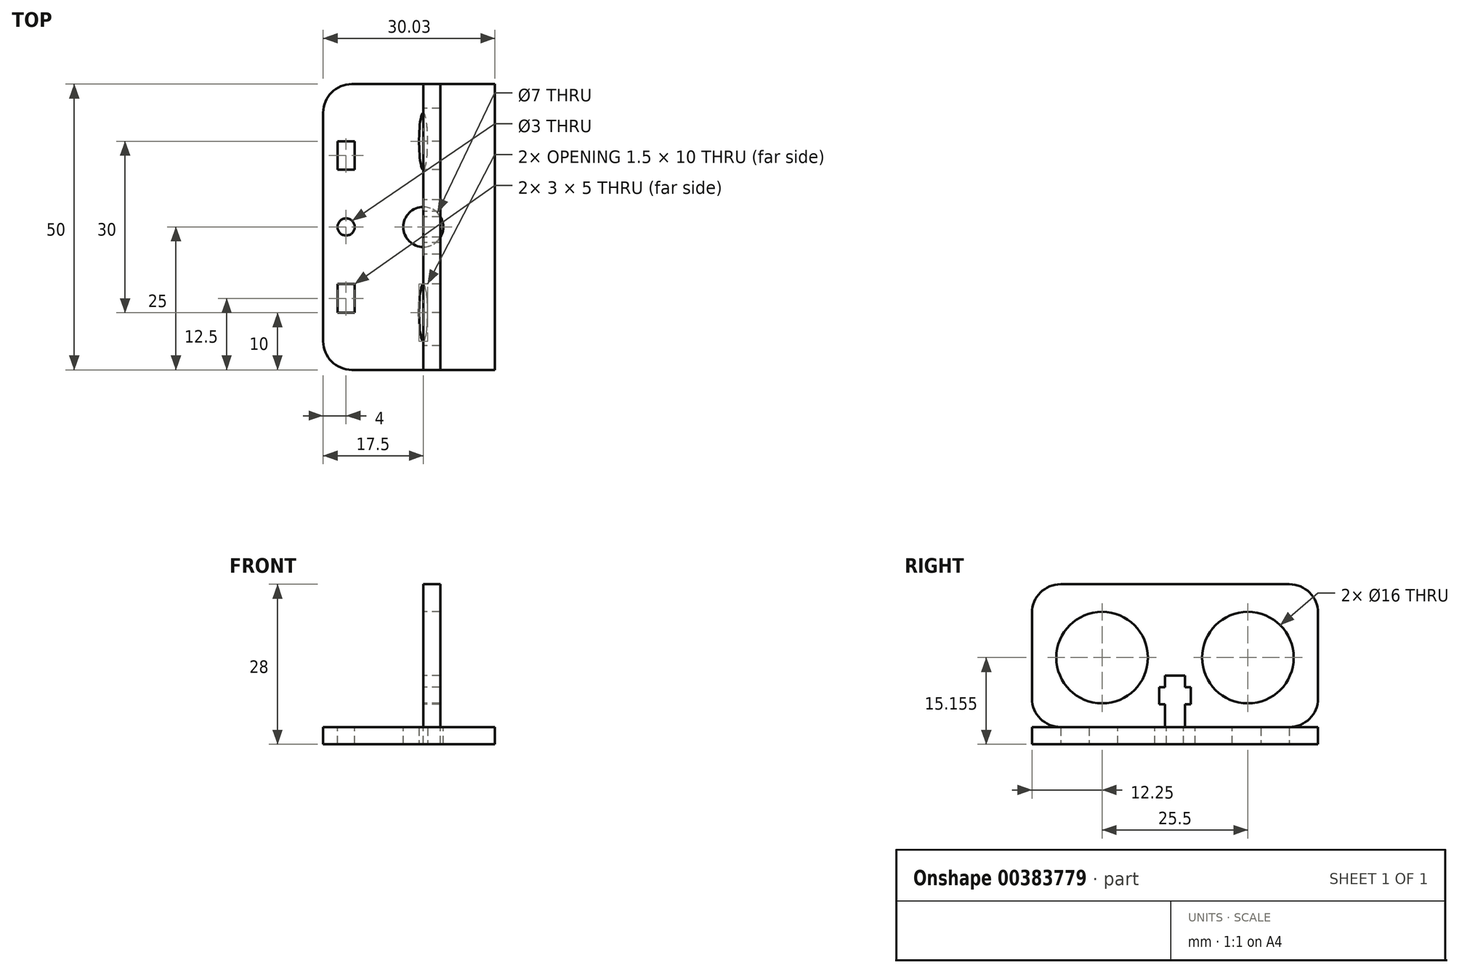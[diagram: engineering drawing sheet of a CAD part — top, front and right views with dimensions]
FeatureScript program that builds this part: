
annotation { "Feature Type Name" : "Feature", "Feature Type Description" : "" }
export const myFeature = defineFeature(function(context is Context, id is Id, definition is map)
    precondition{}
    {
        {
            var Q0;
            Q0=qCreatedBy(makeId("Top.planeOp"),FACE);
            var sketch = newSketch(context, id + "F0", { "sketchPlane" : qUnion([Q0])});
            skLineSegment(sketch, "E0.bottom", {"start": v(-17.5, 25) * mm, "end": v(17.5, 25) * mm});
            skLineSegment(sketch, "E0.top", {"start": v(-17.5, -25) * mm, "end": v(17.5, -25) * mm});
            skLineSegment(sketch, "E0.left", {"start": v(-17.5, 25) * mm, "end": v(-17.5, -25) * mm});
            skLineSegment(sketch, "E0.right", {"start": v(17.5, 25) * mm, "end": v(17.5, -25) * mm});
            skPoint(sketch, "E0.middle", {"position": v(0, 0) * mm});
            skSolve(sketch);
        }
        {
            var Q0;
            Q0=makeQuery(id+"F0.imprint","IMPRINT",FACE,{"disambiguationData":[TD([[makeQuery(id+"F0.imprint","IMPRINT",EDGE,{"derivedFrom":sQuery(id+"F0.wireOp",EDGE,"E0.bottom")}),-1.0]])]});
            extrude(context, id + "F1", {"entities" : qUnion([Q0]), "depth" : 3 * mm});
        }
        {
            var Q0;
            Q0=makeQuery(id+"F1.opExtrude","CAP_FACE",FACE,{"disambiguationData":[OSD([sQuery(id+"F0.wireOp",EDGE,"E0.bottom"),sQuery(id+"F0.wireOp",EDGE,"E0.top"),sQuery(id+"F0.wireOp",EDGE,"E0.left"),sQuery(id+"F0.wireOp",EDGE,"E0.right")])],"isStart":false});
            var sketch = newSketch(context, id + "F2", { "sketchPlane" : qUnion([Q0])});
            skLineSegment(sketch, "E1.bottom", {"start": v(-12, -15) * mm, "end": v(-15, -15) * mm});
            skLineSegment(sketch, "E1.top", {"start": v(-12, -10) * mm, "end": v(-15, -10) * mm});
            skLineSegment(sketch, "E1.left", {"start": v(-12, -15) * mm, "end": v(-12, -10) * mm});
            skLineSegment(sketch, "E1.right", {"start": v(-15, -15) * mm, "end": v(-15, -10) * mm});
            skPoint(sketch, "E1.middle", {"position": v(-13.5, -12.5) * mm});
            skLineSegment(sketch, "E2.MirrorCS", {"start": v(-12, 15) * mm, "end": v(-15, 15) * mm});
            skPoint(sketch, "E3.MirrorP", {"position": v(-13.5, 12.5) * mm});
            skLineSegment(sketch, "E4.MirrorCS", {"start": v(-12, 10) * mm, "end": v(-15, 10) * mm});
            skLineSegment(sketch, "E5.MirrorCS", {"start": v(-15, 15) * mm, "end": v(-15, 10) * mm});
            skLineSegment(sketch, "E6.MirrorCS", {"start": v(-12, 15) * mm, "end": v(-12, 10) * mm});
            skCircle(sketch, "E7", {"center": v(-13.5, 0) * mm, "radius": 1.5 * mm});
            skCircle(sketch, "E8", {"center": v(0, 0) * mm, "radius": 3.5 * mm});
            skLineSegment(sketch, "E9", {"start": v(-13.5, -12.5) * mm, "end": v(-13.5, 12.5) * mm, "construction": true});
            skEllipse(sketch, "E10", {"center": v(0, -15) * mm, "majorRadius": 5 * mm, "minorRadius": 0.75 * mm, "majorAxis": v(0, 1)});
            skEllipse(sketch, "E11.MirrorC", {"center": v(0, 15) * mm, "majorRadius": 5 * mm, "minorRadius": 0.75 * mm, "majorAxis": v(0, -1)});
            skLineSegment(sketch, "E12.bottom", {"start": v(17.5, 25) * mm, "end": v(12.53, 25) * mm});
            skLineSegment(sketch, "E12.top", {"start": v(17.5, -25) * mm, "end": v(12.53, -25) * mm});
            skLineSegment(sketch, "E12.left", {"start": v(17.5, 25) * mm, "end": v(17.5, -25) * mm});
            skLineSegment(sketch, "E12.right", {"start": v(12.53, 25) * mm, "end": v(12.53, -25) * mm});
            skSolve(sketch);
        }
        {
            var Q0;
            Q0 = qSketchRegion(id + "F2", true);
            extrude(context, id + "F3", {"entities" : qUnion([Q0]), "operationType" : NewBodyOperationType.REMOVE, "oppositeDirection" : true, "depth" : 25 * mm});
        }
        {
            var Q0;
            Q0=qCreatedBy(makeId("Right.planeOp"),FACE);
            var sketch = newSketch(context, id + "F4", { "sketchPlane" : qUnion([Q0])});
            skLineSegment(sketch, "E13.bottom", {"start": v(-25, 3) * mm, "end": v(-15, 3) * mm});
            skLineSegment(sketch, "E13.top", {"start": v(-25, 28) * mm, "end": v(25, 28) * mm});
            skLineSegment(sketch, "E13.left", {"start": v(-25, 3) * mm, "end": v(-25, 28) * mm});
            skLineSegment(sketch, "E13.right", {"start": v(25, 3) * mm, "end": v(25, 28) * mm});
            skCircle(sketch, "E14", {"center": v(-12.75, 15.16) * mm, "radius": 8 * mm});
            skCircle(sketch, "E15.MirrorC", {"center": v(12.75, 15.16) * mm, "radius": 8 * mm});
            skLineSegment(sketch, "E16", {"start": v(-15, 3) * mm, "end": v(-15, 0) * mm});
            skLineSegment(sketch, "E17", {"start": v(-15, 0) * mm, "end": v(-10, 0) * mm});
            skLineSegment(sketch, "E18", {"start": v(-10, 0) * mm, "end": v(-10, 3) * mm});
            skLineSegment(sketch, "E19.trimOffspring", {"start": v(-10, 3) * mm, "end": v(10, 3) * mm});
            skLineSegment(sketch, "E20.MirrorCS", {"start": v(10, 0) * mm, "end": v(10, 3) * mm});
            skLineSegment(sketch, "E21.MirrorCS", {"start": v(15, 0) * mm, "end": v(10, 0) * mm});
            skLineSegment(sketch, "E22.MirrorCS", {"start": v(15, 3) * mm, "end": v(15, 0) * mm});
            skLineSegment(sketch, "E23.trimOffspring", {"start": v(15, 3) * mm, "end": v(25, 3) * mm});
            skLineSegment(sketch, "E24.bottom", {"start": v(-1.75, 3) * mm, "end": v(1.75, 3) * mm});
            skLineSegment(sketch, "E24.top", {"start": v(-1.75, 12) * mm, "end": v(1.75, 12) * mm});
            skLineSegment(sketch, "E24.left", {"start": v(-1.75, 3) * mm, "end": v(-1.75, 7) * mm});
            skLineSegment(sketch, "E24.right", {"start": v(1.75, 3) * mm, "end": v(1.75, 7) * mm});
            skLineSegment(sketch, "E25.bottom", {"start": v(-2.75, 7) * mm, "end": v(-1.75, 7) * mm});
            skLineSegment(sketch, "E25.top", {"start": v(-2.75, 10) * mm, "end": v(-1.75, 10) * mm});
            skLineSegment(sketch, "E25.left", {"start": v(-2.75, 7) * mm, "end": v(-2.75, 10) * mm});
            skLineSegment(sketch, "E25.right", {"start": v(2.75, 7) * mm, "end": v(2.75, 10) * mm});
            skLineSegment(sketch, "E26.trimOffspring", {"start": v(1.75, 10) * mm, "end": v(2.75, 10) * mm});
            skLineSegment(sketch, "E27.trimOffspring", {"start": v(-1.75, 10) * mm, "end": v(-1.75, 12) * mm});
            skLineSegment(sketch, "E28.trimOffspring", {"start": v(1.75, 10) * mm, "end": v(1.75, 12) * mm});
            skLineSegment(sketch, "E29.trimOffspring", {"start": v(1.75, 7) * mm, "end": v(2.75, 7) * mm});
            skSolve(sketch);
        }
        {
            var Q0;
            Q0=makeQuery(id+"F4.imprint","IMPRINT",FACE,{"disambiguationData":[TD([[makeQuery(id+"F4.imprint","IMPRINT",EDGE,{"derivedFrom":sQuery(id+"F4.wireOp",EDGE,"E13.bottom")}),1.0]])]});
            extrude(context, id + "F5", {"entities" : qUnion([Q0]), "depth" : 3 * mm});
        }
        {
            var Q0;
            Q0=makeQuery(id+"F3.boolean.opBoolean","COPY",EDGE,{"derivedFrom":makeQuery(id+"F3.opExtrude","SWEPT_EDGE",EDGE,{"disambiguationData":[OSD([sQuery(id+"F0.wireOp",EDGE,"E0.bottom"),sQuery(id+"F2.wireOp",EDGE,"E12.bottom"),sQuery(id+"F2.wireOp",EDGE,"E12.right")])]})});
            var Q1;
            Q1=makeQuery(id+"F3.boolean.opBoolean","COPY",EDGE,{"derivedFrom":makeQuery(id+"F3.opExtrude","SWEPT_EDGE",EDGE,{"disambiguationData":[OSD([sQuery(id+"F0.wireOp",EDGE,"E0.top"),sQuery(id+"F2.wireOp",EDGE,"E12.top"),sQuery(id+"F2.wireOp",EDGE,"E12.right")])]})});
            var Q2;
            Q2=makeQuery(id+"F1.opExtrude","SWEPT_EDGE",EDGE,{"disambiguationData":[OSD([sQuery(id+"F0.wireOp",EDGE,"E0.top"),sQuery(id+"F0.wireOp",EDGE,"E0.left")])]});
            var Q3;
            Q3=makeQuery(id+"F1.opExtrude","SWEPT_EDGE",EDGE,{"disambiguationData":[OSD([sQuery(id+"F0.wireOp",EDGE,"E0.bottom"),sQuery(id+"F0.wireOp",EDGE,"E0.left")])]});
            fillet(context, id + "F6", {"entities" : qUnion([Q0, Q1, Q2, Q3]), "radius" : 5 * mm, "tangentPropagation" : true, "allowEdgeOverflow" : false});
        }
        {
            var Q0;
            Q0=makeQuery(id+"F5.opExtrude","SWEPT_EDGE",EDGE,{"disambiguationData":[OSD([sQuery(id+"F4.wireOp",EDGE,"E13.bottom"),sQuery(id+"F4.wireOp",EDGE,"E13.left")])]});
            var Q1;
            Q1=makeQuery(id+"F5.opExtrude","SWEPT_EDGE",EDGE,{"disambiguationData":[OSD([sQuery(id+"F4.wireOp",EDGE,"E13.top"),sQuery(id+"F4.wireOp",EDGE,"E13.left")])]});
            var Q2;
            Q2=makeQuery(id+"F5.opExtrude","SWEPT_EDGE",EDGE,{"disambiguationData":[OSD([sQuery(id+"F4.wireOp",EDGE,"E13.top"),sQuery(id+"F4.wireOp",EDGE,"E13.right")])]});
            var Q3;
            Q3=makeQuery(id+"F5.opExtrude","SWEPT_EDGE",EDGE,{"disambiguationData":[OSD([sQuery(id+"F4.wireOp",EDGE,"E13.right"),sQuery(id+"F4.wireOp",EDGE,"E23.trimOffspring")])]});
            fillet(context, id + "F7", {"entities" : qUnion([Q0, Q1, Q2, Q3]), "radius" : 5 * mm, "tangentPropagation" : true, "allowEdgeOverflow" : false});
        }
    });
